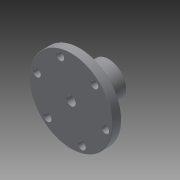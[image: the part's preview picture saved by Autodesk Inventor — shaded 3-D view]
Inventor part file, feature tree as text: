
AUTODESK INVENTOR PART (.ipt)
format: ipt  version: 2014 (Build 180170000, 170)  size: 381,440 bytes
history: native  units: mm
features: fillet x17, sketch x8, extrude x5, plane x2, pattern_circular x1, hole x1, other x1
ambient origin geometry x8: Origin, YZ Plane, XZ Plane, XY Plane, X Axis, Y Axis, Z Axis, Center Point
bodies: Volumenkörper1 (feature_tree)
feature tree (35):
  extrude  "Extrusion1"  Depth=6.0mm TaperAngle=0.0deg
  extrude  "Extrusion2"  Depth=48.0mm
  pattern_circular  "Runde Anordnung1"  Count=6 Angle=360.0deg
  extrude  "Extrusion3"  Depth=20.0mm TaperAngle=0.0deg
  extrude  "Extrusion4"  Depth=23.0mm TaperAngle=0.0deg
  fillet  "Rundung1"  Radius=0.25mm
  fillet  "Rundung2"  Radius=0.25mm
  fillet  "Rundung3"  Radius=0.25mm
  fillet  "Rundung4"  Radius=0.25mm
  fillet  "Rundung5"  Radius=0.25mm
  fillet  "Rundung6"  Radius=0.25mm
  fillet  "Rundung7"  Radius=0.25mm
  fillet  "Rundung8"  Radius=0.25mm
  fillet  "Rundung9"  Radius=0.25mm
  fillet  "Rundung10"  Radius=0.25mm
  fillet  "Rundung11"  Radius=0.25mm
  fillet  "Rundung12"  Radius=0.25mm
  fillet  "Rundung13"  Radius=0.25mm
  fillet  "Rundung14"  Radius=0.25mm
  fillet  "Rundung15"  Radius=0.25mm
  fillet  "Rundung16"  Radius=0.25mm
  fillet  "Rundung17"  Radius=0.25mm
  plane  "Arbeitsebene1"
  hole  "Bohrung1"  [1 undecoded]
  plane  "Arbeitsebene2"
  other  "Spirale3"
  extrude  "Extrusion6"  [1 undecoded]
  sketch  "Skizze1"  dims[d0=57.0mm d1=6.0mm d2=0.0mm]
  sketch  "Skizze2"  dims[d3=5.0mm d4=48.0mm]
  sketch  "Skizze3"  dims[d5=6.0mm d6=0.0mm d7=60.0mm d8=360.0deg]
  sketch  "Skizze4"  dims[d10=24.0mm d11=20.0mm d12=0.0mm]
  sketch  "Skizze7"  dims[d13=6.0mm d14=23.0mm d15=0.0mm d16=0.25mm d17=0.25mm d18=0.25mm d19=0.25mm d20=0.25mm d21=0.25mm d22=0.25mm d23=0.25mm d24=0.25mm d25=0.25mm d26=0.25mm d27=0.25mm d28=0.25mm d29=0.25mm d30=0.25mm d31=0.25mm d32=0.25mm]
  sketch  "Skizze12"  dims[d33=12.0mm d35=10.0mm]
  sketch  "Skizze14"  dims[d36=5.0mm d37=6.0mm d38=4.0mm d39=2.0mm d40=90.0deg d41=8.0mm d42=20.594885mm d63=-10.0mm]
  sketch  "Skizze16"  dims[d64=4.5mm d65=60.0deg d66=60.0deg d67=0.005mm d68=0.8mm d69=10.0mm d70=130.0mm d71=0.0mm d72=90.0deg d73=90.0deg d74=0.0mm d75=0.0mm d76=15.0mm d77=0.0mm]
note: 2 required parameter values undecoded (feature->parameter linkage not recoverable at this tier; creation-order binding heuristic only, values carry confidence <= 0.55)
